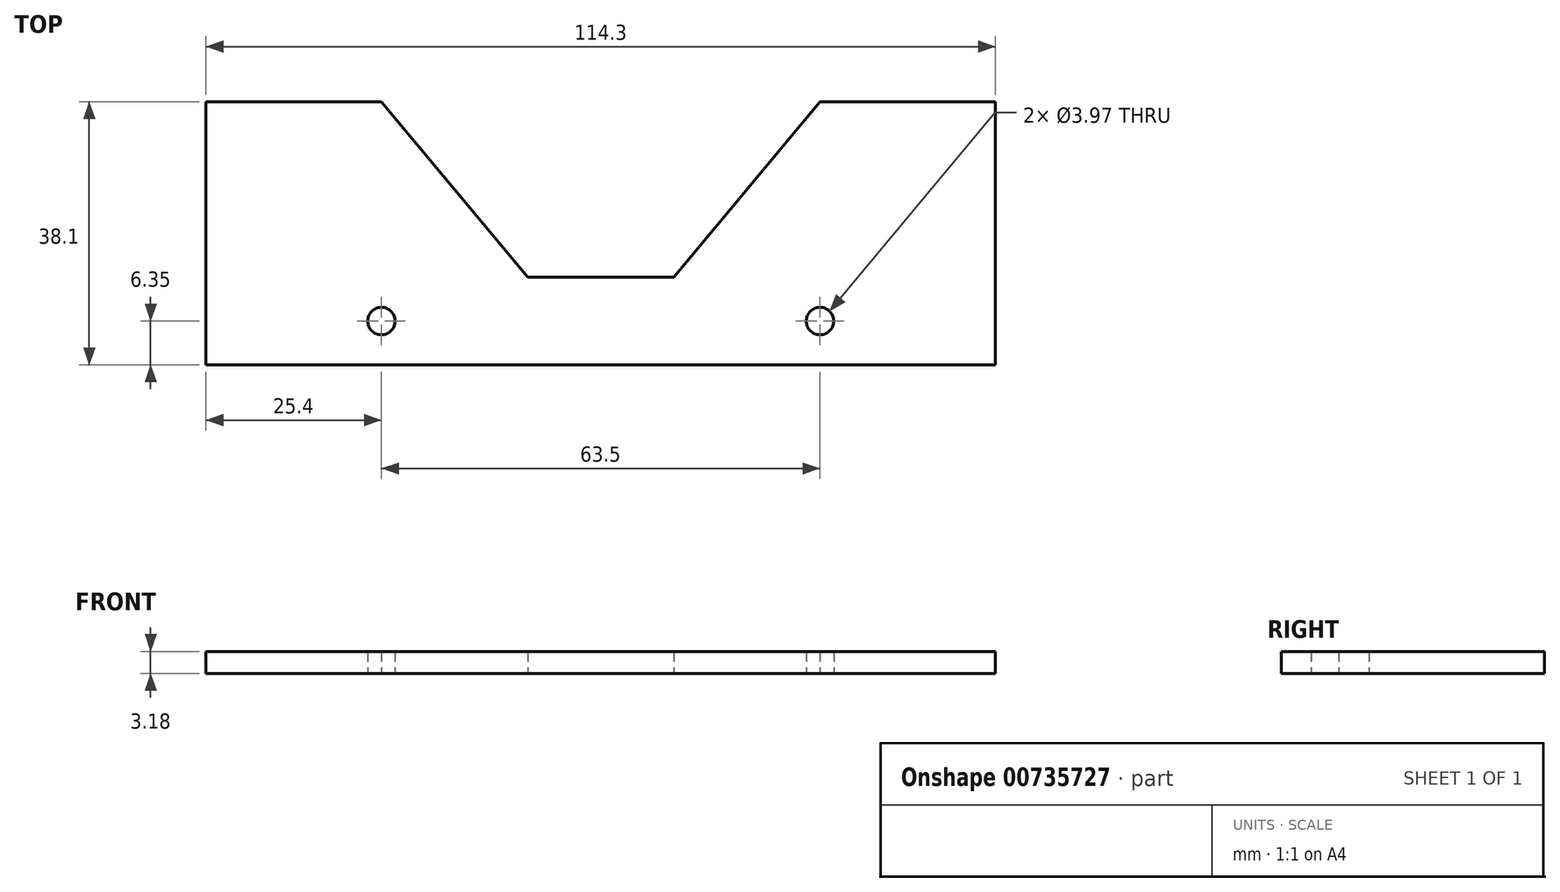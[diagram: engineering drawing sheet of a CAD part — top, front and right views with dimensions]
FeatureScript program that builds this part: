
annotation { "Feature Type Name" : "Feature", "Feature Type Description" : "" }
export const myFeature = defineFeature(function(context is Context, id is Id, definition is map)
    precondition{}
    {
        {
            var Q0;
            Q0=qCreatedBy(makeId("Top.planeOp"),FACE);
            var sketch = newSketch(context, id + "F0", { "sketchPlane" : qUnion([Q0])});
            skLineSegment(sketch, "E0", {"start": v(-57.15, 0) * mm, "end": v(57.15, 0) * mm});
            skLineSegment(sketch, "E1", {"start": v(57.15, 0) * mm, "end": v(0, 0) * mm});
            skLineSegment(sketch, "E2", {"start": v(0, 0) * mm, "end": v(57.15, 0) * mm});
            skLineSegment(sketch, "E3", {"start": v(57.15, 0) * mm, "end": v(57.15, 38.1) * mm});
            skLineSegment(sketch, "E4", {"start": v(57.15, 38.1) * mm, "end": v(31.75, 38.1) * mm});
            skLineSegment(sketch, "E5.MirrorCS", {"start": v(-57.15, 0) * mm, "end": v(-57.15, 38.1) * mm});
            skLineSegment(sketch, "E6.MirrorCS", {"start": v(-57.15, 38.1) * mm, "end": v(-31.75, 38.1) * mm});
            skLineSegment(sketch, "E7", {"start": v(-31.75, 38.1) * mm, "end": v(0, 0) * mm});
            skLineSegment(sketch, "E8", {"start": v(31.75, 38.1) * mm, "end": v(0, 0) * mm});
            skLineSegment(sketch, "E9", {"start": v(0, 0) * mm, "end": v(0, 12.7) * mm});
            skLineSegment(sketch, "E10", {"start": v(0, 12.7) * mm, "end": v(-10.58, 12.7) * mm});
            skLineSegment(sketch, "E11", {"start": v(-10.58, 12.7) * mm, "end": v(10.58, 12.7) * mm});
            skLineSegment(sketch, "E12", {"start": v(-10.58, 12.7) * mm, "end": v(-57.15, 12.7) * mm});
            skLineSegment(sketch, "E13", {"start": v(-57.15, 12.7) * mm, "end": v(57.15, 12.7) * mm});
            skCircle(sketch, "E14", {"center": v(-31.75, 6.35) * mm, "radius": 1.98 * mm});
            skLineSegment(sketch, "E15", {"start": v(0, 0) * mm, "end": v(0, -10.8) * mm});
            skCircle(sketch, "E16.MirrorC", {"center": v(31.75, 6.35) * mm, "radius": 1.98 * mm});
            skSolve(sketch);
        }
        {
            var Q0;
            {var subQ3=sQuery(id+"F0.wireOp",EDGE,"E0");Q0=makeQuery(id+"F0.imprint","IMPRINT",FACE,{"disambiguationData":[TD([[makeQuery(id+"F0.imprint","IMPRINT",EDGE,{"derivedFrom":subQ3}),1.0]])]});}
            var Q1;
            {var subQ0=sQuery(id+"F0.wireOp",EDGE,"E9");Q1=makeQuery(id+"F0.imprint","IMPRINT",FACE,{"disambiguationData":[TD([[makeQuery(id+"F0.imprint","IMPRINT",EDGE,{"derivedFrom":subQ0}),-1.0]])]});}
            var Q2;
            {var subQ0=sQuery(id+"F0.wireOp",EDGE,"E9");Q2=makeQuery(id+"F0.imprint","IMPRINT",FACE,{"disambiguationData":[TD([[makeQuery(id+"F0.imprint","IMPRINT",EDGE,{"derivedFrom":subQ0}),1.0]])]});}
            var Q3;
            {var subQ0=sQuery(id+"F0.wireOp",EDGE,"E4");Q3=makeQuery(id+"F0.imprint","IMPRINT",FACE,{"disambiguationData":[TD([[makeQuery(id+"F0.imprint","IMPRINT",EDGE,{"derivedFrom":subQ0}),1.0]])]});}
            var Q4;
            {var subQ1=sQuery(id+"F0.wireOp",EDGE,"E2");Q4=makeQuery(id+"F0.imprint","IMPRINT",FACE,{"disambiguationData":[TD([[makeQuery(id+"F0.imprint","IMPRINT",EDGE,{"derivedFrom":subQ1}),1.0]])]});}
            var Q5;
            {var subQ0=sQuery(id+"F0.wireOp",EDGE,"E6.MirrorCS");Q5=makeQuery(id+"F0.imprint","IMPRINT",FACE,{"disambiguationData":[TD([[makeQuery(id+"F0.imprint","IMPRINT",EDGE,{"derivedFrom":subQ0}),-1.0]])]});}
            extrude(context, id + "F1", {"entities" : qUnion([Q0, Q1, Q2, Q3, Q4, Q5]), "depth" : 3.17 * mm, "offsetDistance" : 25.4 * mm});
        }
    });
